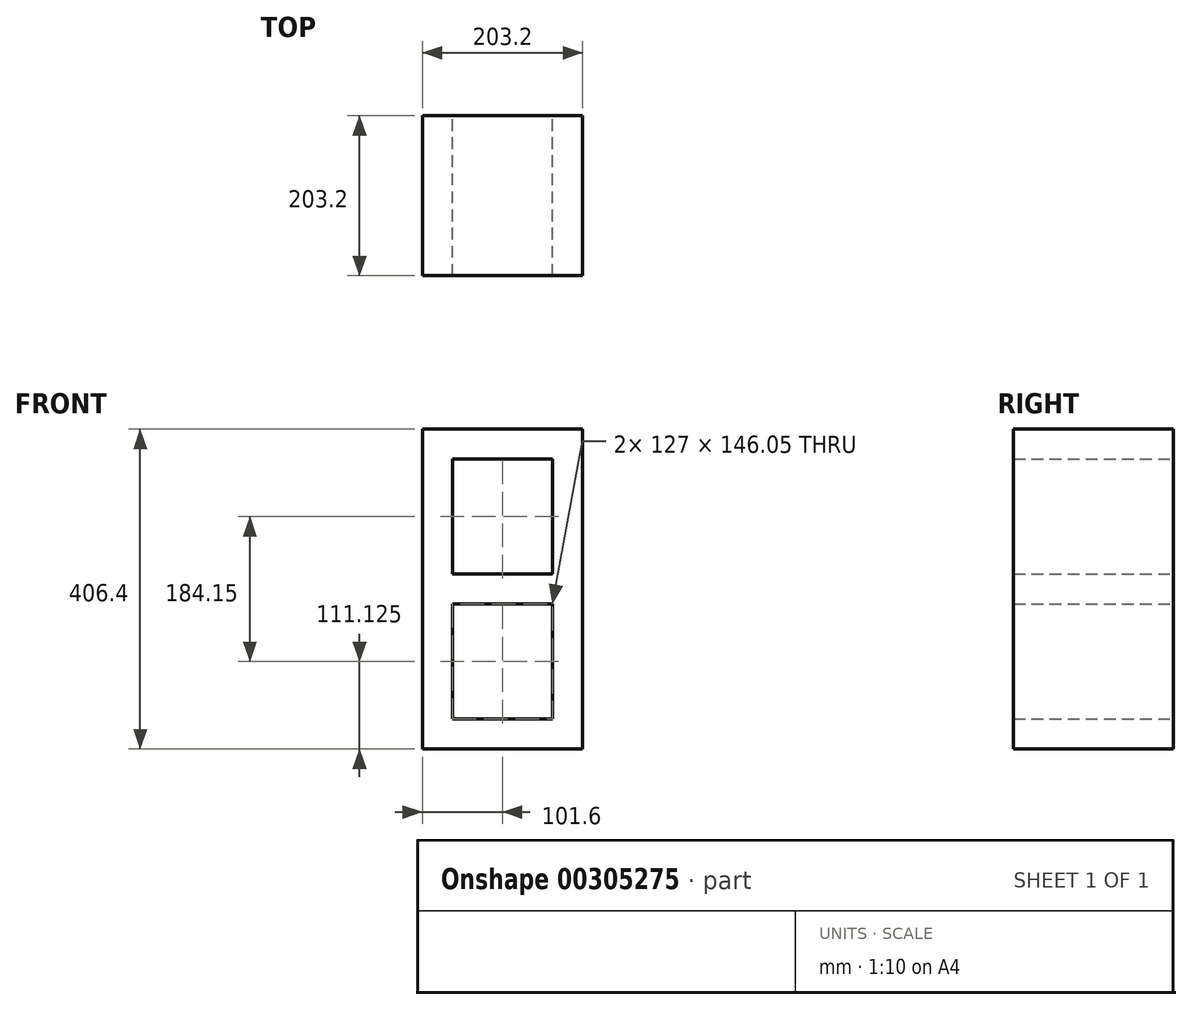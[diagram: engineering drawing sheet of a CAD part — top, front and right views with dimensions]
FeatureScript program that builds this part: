
annotation { "Feature Type Name" : "Feature", "Feature Type Description" : "" }
export const myFeature = defineFeature(function(context is Context, id is Id, definition is map)
    precondition{}
    {
        {
            var Q0;
            Q0=qCreatedBy(makeId("Front.planeOp"),FACE);
            var sketch = newSketch(context, id + "F0", { "sketchPlane" : qUnion([Q0])});
            skLineSegment(sketch, "E0.bottom", {"start": v(-101.6, 203.2) * mm, "end": v(101.6, 203.2) * mm});
            skLineSegment(sketch, "E0.top", {"start": v(-101.6, -203.2) * mm, "end": v(101.6, -203.2) * mm});
            skLineSegment(sketch, "E0.left", {"start": v(-101.6, 203.2) * mm, "end": v(-101.6, -203.2) * mm});
            skLineSegment(sketch, "E0.right", {"start": v(101.6, 203.2) * mm, "end": v(101.6, -203.2) * mm});
            skLineSegment(sketch, "E1.bottom", {"start": v(-63.5, 165.1) * mm, "end": v(63.5, 165.1) * mm});
            skLineSegment(sketch, "E1.top", {"start": v(-63.5, 19.05) * mm, "end": v(63.5, 19.05) * mm});
            skLineSegment(sketch, "E1.left", {"start": v(-63.5, 165.1) * mm, "end": v(-63.5, 19.05) * mm});
            skLineSegment(sketch, "E1.right", {"start": v(63.5, 165.1) * mm, "end": v(63.5, 19.05) * mm});
            skLineSegment(sketch, "E2.bottom", {"start": v(-63.5, -19.05) * mm, "end": v(63.5, -19.05) * mm});
            skLineSegment(sketch, "E2.top", {"start": v(-63.5, -165.1) * mm, "end": v(63.5, -165.1) * mm});
            skLineSegment(sketch, "E2.left", {"start": v(-63.5, -19.05) * mm, "end": v(-63.5, -165.1) * mm});
            skLineSegment(sketch, "E2.right", {"start": v(63.5, -19.05) * mm, "end": v(63.5, -165.1) * mm});
            skLineSegment(sketch, "E3", {"start": v(0, 0) * mm, "end": v(0, 263.05) * mm, "construction": true});
            skLineSegment(sketch, "E4", {"start": v(0, 0) * mm, "end": v(252.07, 0) * mm, "construction": true});
            skSolve(sketch);
        }
        {
            var Q0;
            Q0 = qSketchRegion(id + "F0", true);
            extrude(context, id + "F1", {"entities" : qUnion([Q0]), "depth" : 203.2 * mm});
        }
    });
